# Revit family: Windows_Roof-Windows_Lamilux_Glass-Skylight-w-Aluminium-Frame-0
name_source: partatom
category: Windows
revit_build: Autodesk Revit 2015 (Build: 20140606_1530(x64)
units: mm (PartAtom-declared; Revit-internal decimal feet)

## types (1)
- 500 x 1000 x 150 mm
    Analytic Construction = Uncoated double glazing - 1/4 in thick - bluegreen/clear glass
    Assembly Code = B3020110
    Description = CI System Glass Element FE – Variety of transparent design & optimum energy efficiency
CI System Smoke Lift Glass Element FE – individual daylight and smoke ventilation elements for high- class residential and administrative buildings

With the LAMILUX CI System Element F series, we offer you beautifully shaped elements for flat roofs which will allow you to implement all aspects of modern, energy-efficient, design-oriented construction and put ambitious architectural ideas into practice.
The certified SHEV CI System Smoke Lift Glass Element FE according to EN 12101-2 stands out due to excellent heat and sound insulation values and to individually selectable RAL-colors.
    Edition number = 6
    Frame Material = Aluminium - Lamilux - White
    Glazing Material = Glass - Lamilux
    Heat Transfer Coefficient (U) = 1.9873 W/(m²·K)
    Height = 150 mm  [stored 0.492126 ft]
    Keynote = 8600
    Leaf Material = Aluminium - Lamilux - Black
    Length = 500 mm  [stored 1.64042 ft]
    Manufacturer = Lamilux
    Model = Glass Skylight with aluminium frame 0°
    Product Guid = d9f4ee97-1f19-4f61-b28f-e774976be166
    Product data url = https://www.bimobject.com
    Solar Heat Gain Coefficient = 0.5
    Thermal Resistance (R) = 0.5032 (m²·K)/W
    URL = https://www.lamilux.com
    Visual Light Transmittance = 0.67
    Width = 1000 mm  [stored 3.28084 ft]

note: [stored X ft] marks values corroborated as IEEE doubles in the binary element streams (Revit-internal decimal feet)

## geometry (parser evidence)
native form markers: Blend x2, Sweep x11
no freeform markers — native parametric forms only
